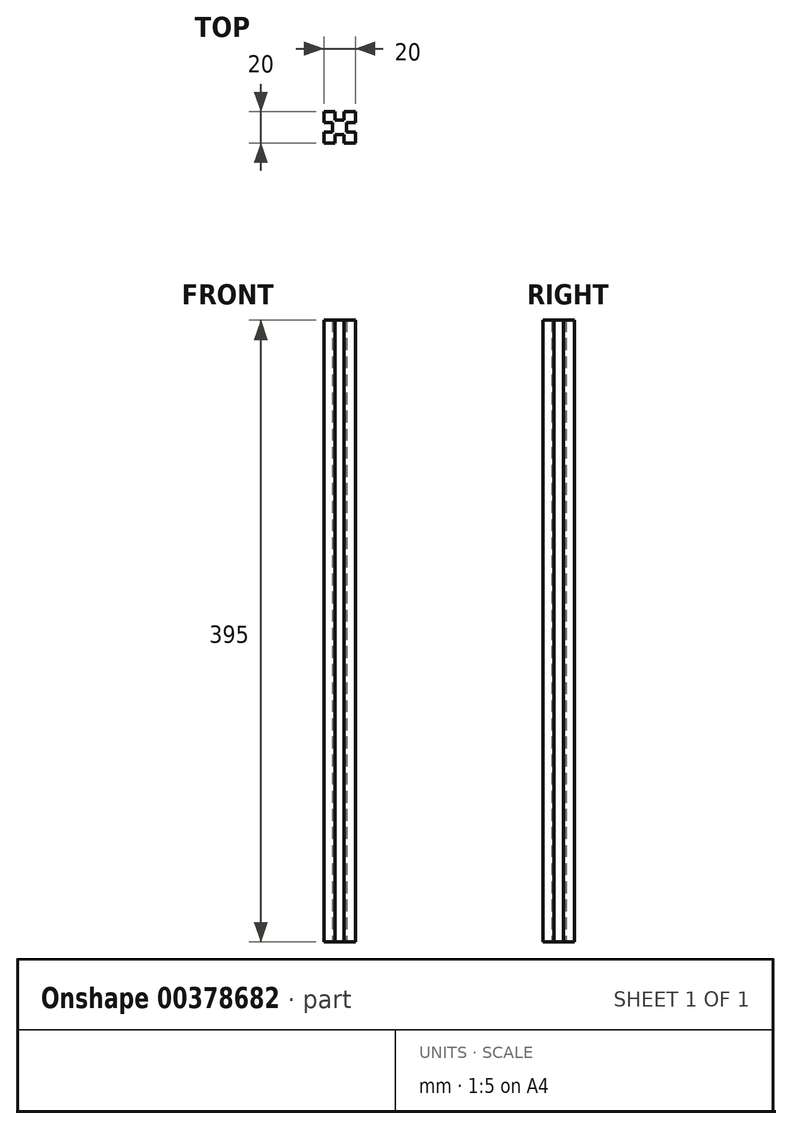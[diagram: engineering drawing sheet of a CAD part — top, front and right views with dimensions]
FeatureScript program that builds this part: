
annotation { "Feature Type Name" : "Feature", "Feature Type Description" : "" }
export const myFeature = defineFeature(function(context is Context, id is Id, definition is map)
    precondition{}
    {
        {
            var Q0;
            Q0=qCreatedBy(makeId("Top.planeOp"),FACE);
            var sketch = newSketch(context, id + "F0", { "sketchPlane" : qUnion([Q0])});
            skLineSegment(sketch, "E0.bottom", {"start": v(0, 0) * mm, "end": v(20, 0) * mm});
            skLineSegment(sketch, "E0.top", {"start": v(0, 20) * mm, "end": v(20, 20) * mm});
            skLineSegment(sketch, "E0.left", {"start": v(0, 0) * mm, "end": v(0, 20) * mm});
            skLineSegment(sketch, "E0.right", {"start": v(20, 0) * mm, "end": v(20, 20) * mm});
            skLineSegment(sketch, "E1.bottom", {"start": v(7, 20) * mm, "end": v(13, 20) * mm});
            skLineSegment(sketch, "E1.top", {"start": v(7, 14.5) * mm, "end": v(13, 14.5) * mm});
            skLineSegment(sketch, "E1.left", {"start": v(7, 20) * mm, "end": v(7, 14.5) * mm});
            skLineSegment(sketch, "E1.right", {"start": v(13, 20) * mm, "end": v(13, 14.5) * mm});
            skLineSegment(sketch, "E2.bottom", {"start": v(20, 13) * mm, "end": v(14.5, 13) * mm});
            skLineSegment(sketch, "E2.top", {"start": v(20, 7) * mm, "end": v(14.5, 7) * mm});
            skLineSegment(sketch, "E2.left", {"start": v(20, 13) * mm, "end": v(20, 7) * mm});
            skLineSegment(sketch, "E2.right", {"start": v(14.5, 13) * mm, "end": v(14.5, 7) * mm});
            skLineSegment(sketch, "E3.bottom", {"start": v(13, 0) * mm, "end": v(7, 0) * mm});
            skLineSegment(sketch, "E3.top", {"start": v(13, 5.5) * mm, "end": v(7, 5.5) * mm});
            skLineSegment(sketch, "E3.left", {"start": v(13, 0) * mm, "end": v(13, 5.5) * mm});
            skLineSegment(sketch, "E3.right", {"start": v(7, 0) * mm, "end": v(7, 5.5) * mm});
            skLineSegment(sketch, "E4.bottom", {"start": v(0, 7) * mm, "end": v(5.5, 7) * mm});
            skLineSegment(sketch, "E4.top", {"start": v(0, 13) * mm, "end": v(5.5, 13) * mm});
            skLineSegment(sketch, "E4.left", {"start": v(0, 7) * mm, "end": v(0, 13) * mm});
            skLineSegment(sketch, "E4.right", {"start": v(5.5, 7) * mm, "end": v(5.5, 13) * mm});
            skSolve(sketch);
        }
        {
            var Q0;
            Q0=makeQuery(id+"F0.imprint","IMPRINT",FACE,{"disambiguationData":[TD([[makeQuery(id+"F0.imprint","IMPRINT",EDGE,{"derivedFrom":sQuery(id+"F0.wireOp",EDGE,"E1.top")}),-1.0]])]});
            extrude(context, id + "F1", {"entities" : qUnion([Q0]), "depth" : 395 * mm});
        }
    });
